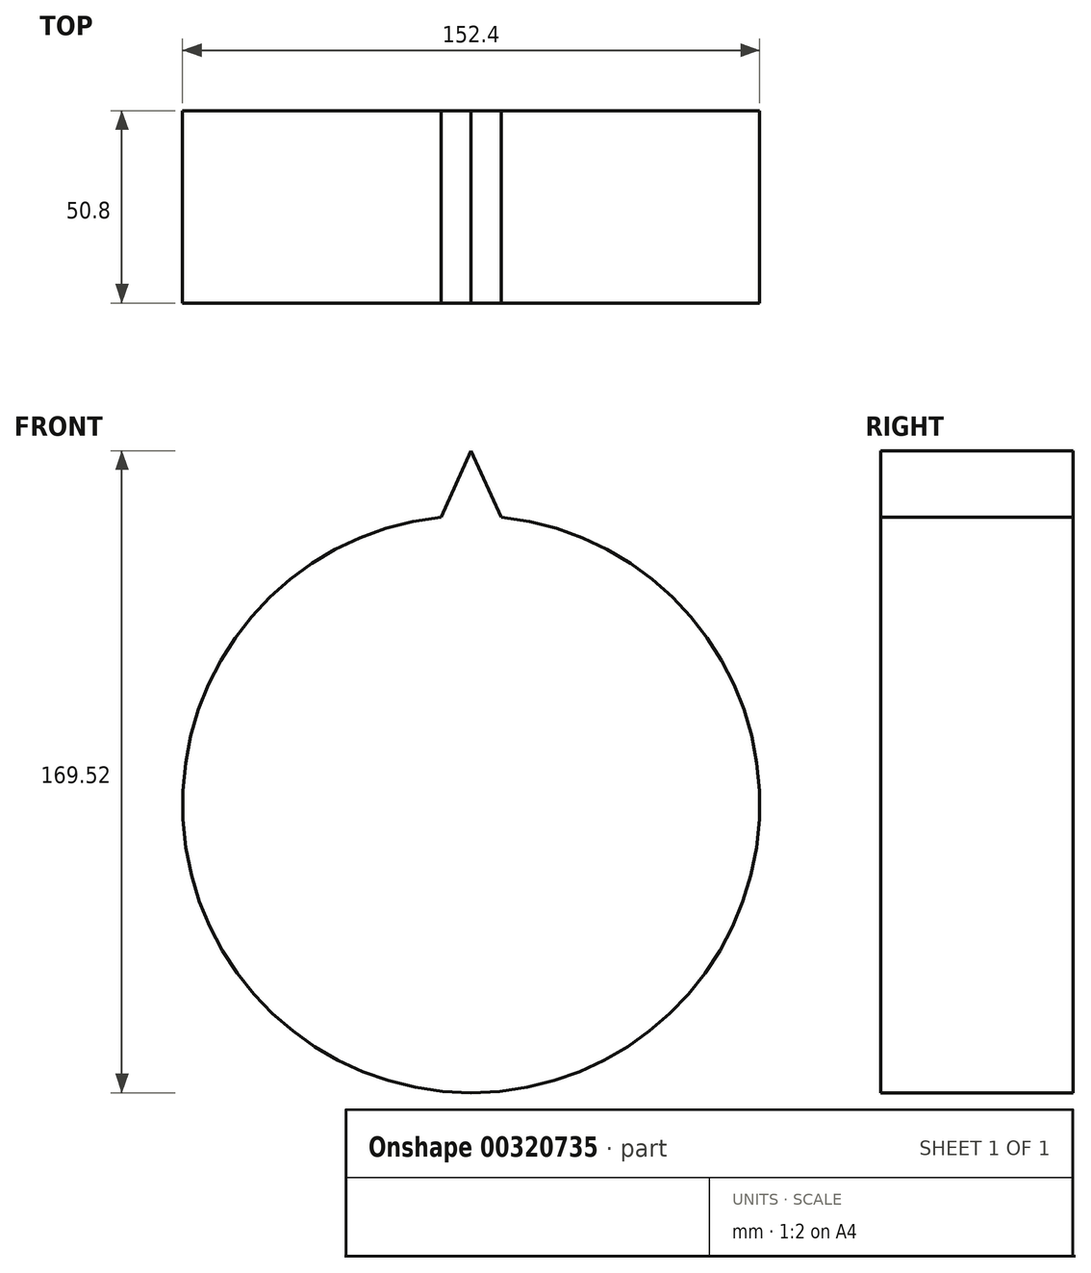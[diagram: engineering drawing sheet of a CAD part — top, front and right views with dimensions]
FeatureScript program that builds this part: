
annotation { "Feature Type Name" : "Feature", "Feature Type Description" : "" }
export const myFeature = defineFeature(function(context is Context, id is Id, definition is map)
    precondition{}
    {
        {
            var Q0;
            Q0=qCreatedBy(makeId("Front.planeOp"),FACE);
            var sketch = newSketch(context, id + "F0", { "sketchPlane" : qUnion([Q0])});
            skCircle(sketch, "E0", {"center": v(0, 0) * mm, "radius": 76.2 * mm});
            skSolve(sketch);
        }
        {
            var Q0;
            Q0=makeQuery(id+"F0.imprint","IMPRINT",FACE,{"disambiguationData":[TD([[makeQuery(id+"F0.imprint","IMPRINT",EDGE,{"derivedFrom":sQuery(id+"F0.wireOp",EDGE,"E0")}),1.0]])]});
            extrude(context, id + "F1", {"entities" : qUnion([Q0]), "depth" : 50.8 * mm, "symmetric" : true});
        }
        {
            var Q0;
            Q0=makeQuery(id+"F1.opExtrude","CAP_FACE",FACE,{"disambiguationData":[OSD([sQuery(id+"F0.wireOp",EDGE,"E0")])],"isStart":false});
            var sketch = newSketch(context, id + "F2", { "sketchPlane" : qUnion([Q0])});
            skLineSegment(sketch, "E1", {"start": v(-8, 75.78) * mm, "end": v(0, 93.32) * mm});
            skLineSegment(sketch, "E2", {"start": v(0, 93.32) * mm, "end": v(8, 75.78) * mm});
            skArc(sketch, "E3.0", {"start": v(8, 75.78) * mm, "mid": v(0, 76.2) * mm, "end": v(-8, 75.78) * mm});
            skSolve(sketch);
        }
        {
            var Q0;
            Q0 = qSketchRegion(id + "F2", true);
            var Q1;
            Q1=makeQuery(id+"F1.opExtrude","CAP_FACE",FACE,{"disambiguationData":[OSD([sQuery(id+"F0.wireOp",EDGE,"E0")])],"isStart":true});
            extrude(context, id + "F3", {"entities" : qUnion([Q0]), "operationType" : NewBodyOperationType.ADD, "endBound" : BoundingType.UP_TO_SURFACE, "oppositeDirection" : true, "endBoundEntityFace" : qUnion([Q1]), "depth" : 25.4 * mm});
        }
    });
